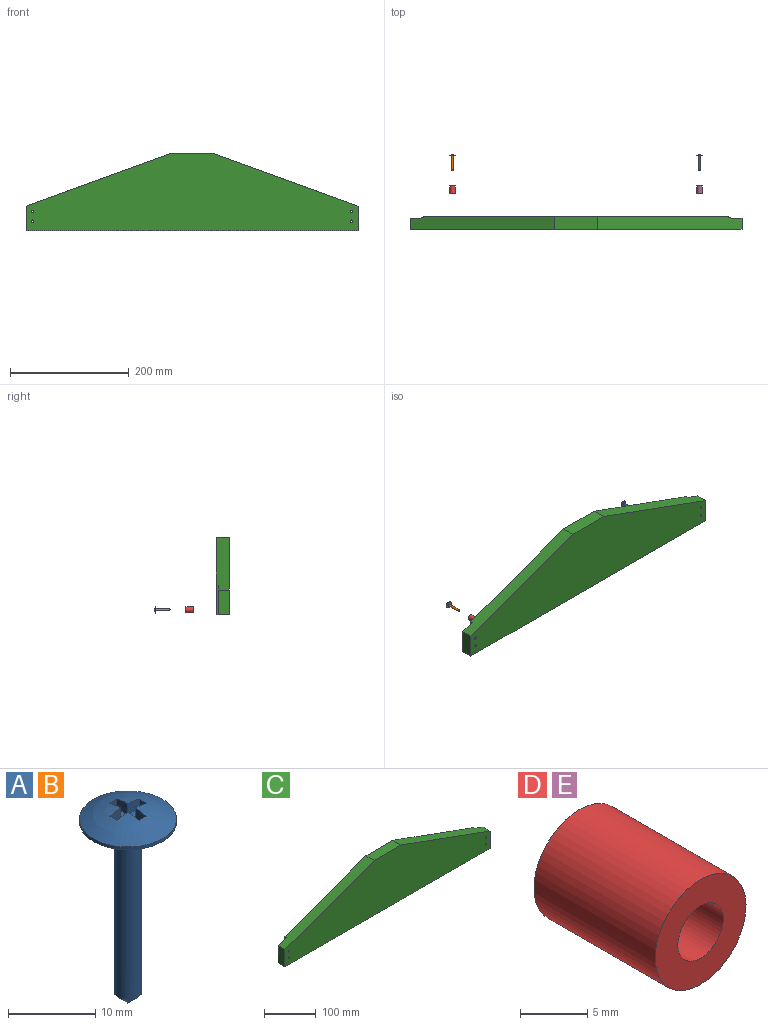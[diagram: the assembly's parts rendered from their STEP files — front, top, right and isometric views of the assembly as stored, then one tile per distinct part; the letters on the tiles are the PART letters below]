
ASSEMBLY  parts=5 mates=4
PART A: 18 faces, bbox 11.1x11.1x27.4 mm
  f0: sphere r=10.52mm, area 94.9mm2, adj f1,f5,f6,f7,f8,f9,f10,f11
  f1: cylinder r=5.56mm len=11.11mm, axis (0,0,-1), area 13.9mm2, adj f0,f2
  f2: plane 11.11x11.11mm, normal (0,0,-1), area 89.1mm2, adj f1,f3
  f3: cylinder r=1.59mm len=23.81mm, axis (0,0,-1), area 237.5mm2, adj f2,f4
  f4: cone r=1.59mm half-angle=45deg, axis (0,0,1), area 11.2mm2, adj f3
  f5: plane 1.31x1.19mm, normal (0,-1,0), area 1.6mm2, adj f0,f6,f16,f17
  f6: plane 1.79x1.55mm, normal (1,0,0), area 2.6mm2, adj f0,f5,f7,f17
  f7: plane 1.79x1.55mm, normal (0,-1,0), area 2.6mm2, adj f0,f6,f8,f17
  f8: plane 1.31x1.19mm, normal (1,0,0), area 1.6mm2, adj f0,f7,f9,f17
  f9: plane 1.79x1.55mm, normal (0,1,0), area 2.6mm2, adj f0,f8,f10,f17
  f10: plane 1.79x1.55mm, normal (1,0,0), area 2.6mm2, adj f0,f9,f11,f17
  f11: plane 1.31x1.19mm, normal (0,1,0), area 1.6mm2, adj f0,f10,f12,f17
  f12: plane 1.79x1.55mm, normal (-1,0,0), area 2.6mm2, adj f0,f11,f13,f17
  f13: plane 1.79x1.55mm, normal (0,1,0), area 2.6mm2, adj f0,f12,f14,f17
  f14: plane 1.31x1.19mm, normal (-1,0,0), area 1.6mm2, adj f0,f13,f15,f17
  f15: plane 1.79x1.55mm, normal (0,-1,0), area 2.6mm2, adj f0,f14,f16,f17
  f16: plane 1.79x1.55mm, normal (-1,0,0), area 2.6mm2, adj f0,f5,f15,f17
  f17: plane 4.76x4.76mm, normal (0,0,1), area 9.9mm2, adj f5,f6,f7,f8,f9,f10,f11,f12
PART B: same geometry as A
PART C: 20 faces, bbox 558.8x22.2x129.7 mm
  f0: plane 558.8x22.23mm, normal (0,0,-1), area 12278.2mm2, adj f1,f3,f4,f7,f8,f9,f10,f11
  f1: plane 514.35x129.68mm, normal (0,1,0), area 48953.1mm2, adj f0,f2,f5,f6,f8,f10,f17,f19
  f2: plane 242.89x88.4mm, normal (-0.34,0,0.94), area 5669.5mm2, adj f1,f3,f6,f7,f10,f11
  f3: plane 41.28x19.05mm, normal (-1,0,0), area 786.3mm2, adj f0,f2,f7,f11
  f4: plane 41.28x19.05mm, normal (1,0,0), area 786.3mm2, adj f0,f5,f7,f9
  f5: plane 242.89x88.4mm, normal (0.34,0,0.94), area 5669.5mm2, adj f1,f4,f6,f7,f8,f9
  f6: plane 73.03x22.23mm, normal (0,0,1), area 1623mm2, adj f1,f2,f5,f7
  f7: plane 558.8x129.68mm, normal (0,-1,0), area 50942.9mm2, adj f0,f2,f3,f4,f5,f6,f12,f13
  f8: plane 49.36x3.18mm, normal (1,0,0), area 156.7mm2, adj f0,f1,f5,f9
  f9: plane 49.36x22.23mm, normal (0,1,0), area 982.5mm2, adj f0,f4,f5,f8,f12,f13
  f10: plane 49.36x3.18mm, normal (-1,0,0), area 156.7mm2, adj f0,f1,f2,f11
  f11: plane 49.36x22.23mm, normal (0,1,0), area 982.5mm2, adj f0,f2,f3,f10,f14,f15
  f12: cylinder r=1.98mm len=19.05mm, axis (0,1,0), area 237.5mm2, adj f7,f9
  f13: cylinder r=1.98mm len=19.05mm, axis (0,1,0), area 237.5mm2, adj f7,f9
  f14: cylinder r=1.98mm len=19.05mm, axis (0,1,0), area 237.5mm2, adj f7,f11
  f15: cylinder r=1.98mm len=19.05mm, axis (0,1,0), area 237.5mm2, adj f7,f11
  f16: cone r=0mm half-angle=59deg, axis (0,1,0), area 14.4mm2, adj f17
  f17: cylinder r=1.98mm len=12.7mm, axis (0,1,0), area 158.3mm2, adj f1,f16
  f18: cone r=0mm half-angle=59deg, axis (0,1,0), area 14.4mm2, adj f19
  f19: cylinder r=1.98mm len=12.7mm, axis (0,1,0), area 158.3mm2, adj f1,f18
PART D: 4 faces, bbox 9.5x12.7x9.5 mm
  f0: cylinder r=2.38mm len=12.7mm, axis (0,1,0), area 190mm2, adj f2,f3
  f1: cylinder r=4.76mm len=12.7mm, axis (0,1,0), area 380mm2, adj f2,f3
  f2: plane 9.53x9.53mm, normal (0,-1,0), area 53.4mm2, adj f0,f1
  f3: plane 9.53x9.53mm, normal (0,1,0), area 53.4mm2, adj f0,f1
PART E: same geometry as D
PLACE A rot(axis=(-1,0,0),90deg) t=(177.01,102,-12.7)mm
PLACE B rot(axis=(-1,0,0),90deg) t=(-238.92,102,-12.7)mm
PLACE C at identity fixed
PLACE D rot(axis=(1,0,0),180deg) t=(-207.96,38.1,-12.7)mm
PLACE E t=(207.96,50.8,-12.7)mm
MATE fastened D.f0 <-> C.f16  axis (0,-1,0) through (-207.96,38.1,-12.7)mm
MATE fastened A.f1 <-> E.f1  axis (0,-1,0) through (207.96,101.6,-12.7)mm
MATE fastened E.f1 <-> C.f18  axis (0,-1,0) through (207.96,38.1,-12.7)mm
MATE fastened B.f1 <-> D.f1  axis (0,-1,0) through (-207.96,101.6,-12.7)mm
